# Revit family: Hinge_74108325T_SureClose-ReadyFit_DD-Technologies
name_source: partatom
category: Specialty Equipment
units: mm (PartAtom-declared; Revit-internal decimal feet)

## family parameters
Cut with Voids When Loaded = No
Enable Cutting in Views = No
Host = Face
Maintain Annotation Orientation = No
Part Type = Normal
Room Calculation Point = No
Round Connector Dimension = Use Diameter
Shared = No

## types (1)
- 74108325T - SureClose® ReadyFit 108 with Safety Feature
    Accessibility = Suitable for ADA applications
    Assembly Code = G2060.20 Fences and Gates
    Catalog Page = https://us.ddtech.com
    Closing Speed = Yes (88°- 0°) And Adjustable
    Colors = Black
    Default Elevation = 0' - 0"
    Description = Externally mounted, hydraulic self-closing hinge-closer, with safety (SF) feature, steel bracket, ADA suitable
    Gate Hardware = Hinge-Closers
    Gate Material = Aluminum, Steel/Ornamental Iron
    Hinge Material = Steel Mounting Brackets (Passivated Zinc Coating), Aluminum Hinge Body
    Hold-Open = No
    Horizontal Gap Adjustment (Variance) = 1/2" - 1 3/8" ( 12 -35mm)
    Keynote = 32 31 00 Fence & Gates
    Latching Speed = Yes (12°- 0°) And Adjustable
    Manufacturer = D&D Technologies
    Max. Opening Angle (Approx.) (Constrained to 0 - 88 degrees) = 0.00°
    Max. Opening Angle (Approx.) (Set In Range 0 - 88°) = 0.00°
    Maximal Self-Closing Gate Weight*  (per pair of hinge) = Up to 260 lb (120 kg) for 74108325T + 74108325T
    Minimum Post Width = 0' - 1 31/32"
    Model = 74108325T
    Product Name = SureClose® ReadyFit 108 with Safety Feature
    Product Webpage with product image = https://us.ddtech.com
    Self-Closing Angle (Approx.) = 88° - 0°
    Specification = https://us.ddtech.com
    Type = Externally Mounted, Hydraulic Self-Closing Hinge-Closer
    URL = https://ddtech.com
    Vertical Adjustment = Yes, through fastener slots

## geometry (parser evidence)
native form markers: Sweep x16
no freeform markers — native parametric forms only
